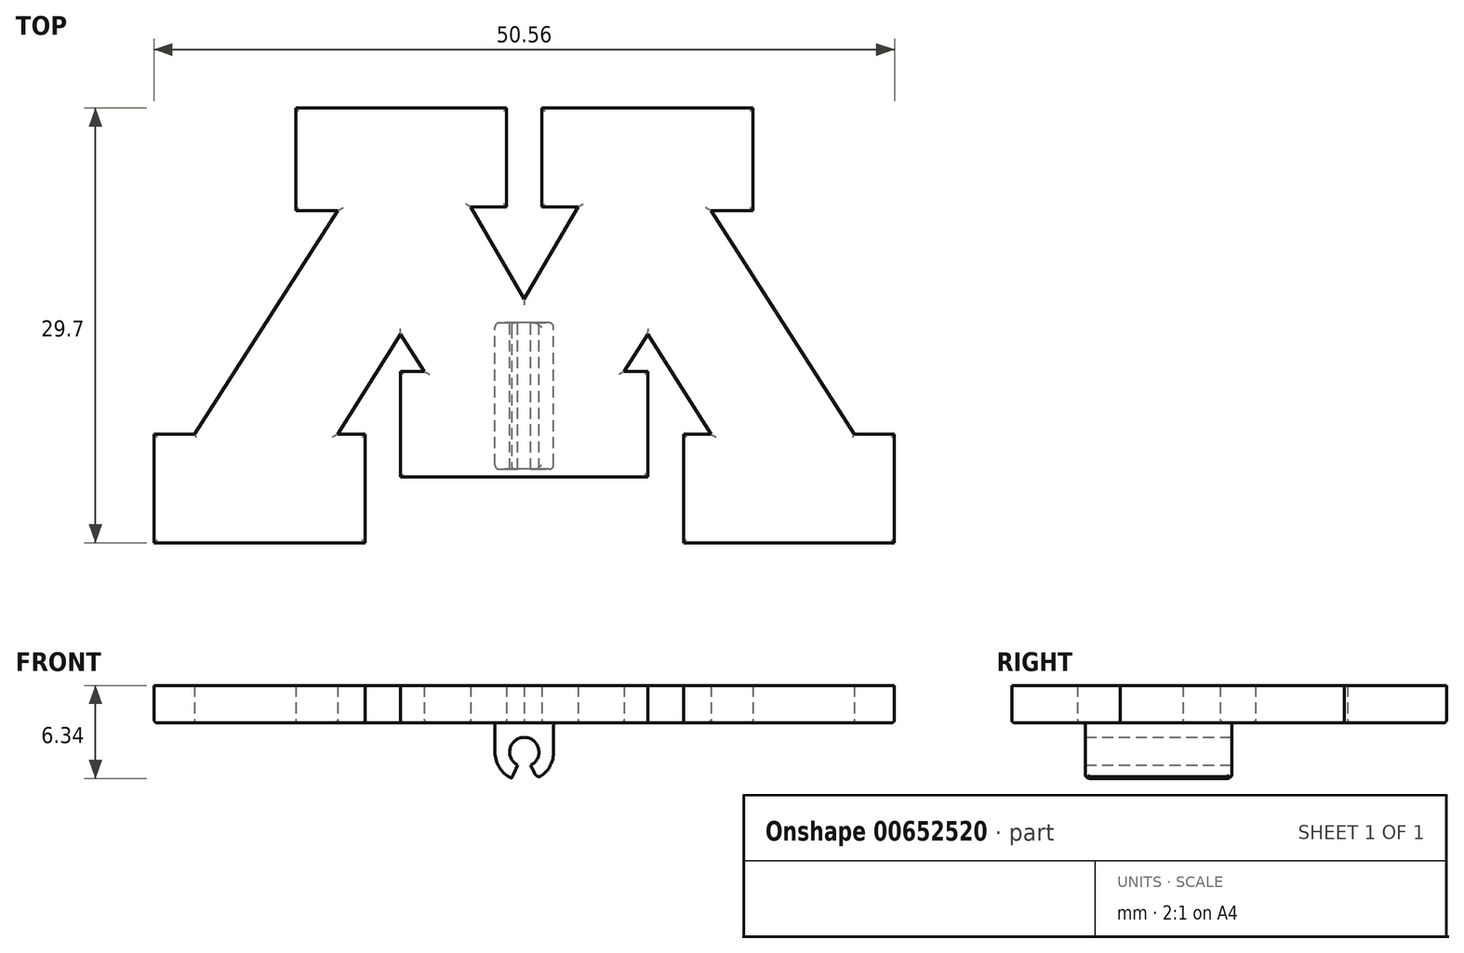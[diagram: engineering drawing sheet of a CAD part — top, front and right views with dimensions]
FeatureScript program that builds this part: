
annotation { "Feature Type Name" : "Feature", "Feature Type Description" : "" }
export const myFeature = defineFeature(function(context is Context, id is Id, definition is map)
    precondition{}
    {
        {
            var Q0;
            Q0=qCreatedBy(makeId("Front.planeOp"),FACE);
            var sketch = newSketch(context, id + "F0", { "sketchPlane" : qUnion([Q0])});
            skCircle(sketch, "E0", {"center": v(0, 0) * mm, "radius": 1 * mm});
            skArc(sketch, "E1", {"start": v(-2, 0) * mm, "mid": v(0, -2) * mm, "end": v(2, 0) * mm});
            skLineSegment(sketch, "E2", {"start": v(-2, 0) * mm, "end": v(-2, 2) * mm});
            skLineSegment(sketch, "E3", {"start": v(-2, 2) * mm, "end": v(0, 2) * mm});
            skLineSegment(sketch, "E4.MirrorCS", {"start": v(2, 2) * mm, "end": v(0, 2) * mm});
            skLineSegment(sketch, "E5.MirrorCS", {"start": v(2, 0) * mm, "end": v(2, 2) * mm});
            skSolve(sketch);
        }
        {
            var Q0;
            Q0=makeQuery(id+"F0.imprint","IMPRINT",FACE,{"disambiguationData":[TD([[makeQuery(id+"F0.imprint","IMPRINT",EDGE,{"derivedFrom":sQuery(id+"F0.wireOp",EDGE,"E0")}),-1.0]])]});
            extrude(context, id + "F1", {"entities" : qUnion([Q0]), "endBound" : BoundingType.SYMMETRIC, "depth" : 10 * mm, "offsetDistance" : 25.4 * mm});
        }
        {
            var Q0;
            Q0=makeQuery(id+"F1.opExtrude","CAP_FACE",FACE,{"disambiguationData":[OSD([sQuery(id+"F0.wireOp",EDGE,"E0"),sQuery(id+"F0.wireOp",EDGE,"E1")])],"isStart":false});
            var sketch = newSketch(context, id + "F2", { "sketchPlane" : qUnion([Q0])});
            skLineSegment(sketch, "E6", {"start": v(0, 0) * mm, "end": v(-0.87, -1.8) * mm});
            skLineSegment(sketch, "E7.MirrorCS", {"start": v(0, 0) * mm, "end": v(0.87, -1.8) * mm});
            skArc(sketch, "E8", {"start": v(-0.87, -1.8) * mm, "mid": v(0, -2) * mm, "end": v(0.87, -1.8) * mm});
            skSolve(sketch);
        }
        {
            var Q0;
            Q0=qSketchRegion(id+"F2",true);
            extrude(context, id + "F3", {"entities" : qUnion([Q0]), "operationType" : NewBodyOperationType.REMOVE, "endBound" : BoundingType.THROUGH_ALL, "oppositeDirection" : true, "depth" : 25 * mm, "offsetDistance" : 25 * mm});
        }
        {
            var Q0;
            Q0=makeQuery(id+"F3.boolean.opBoolean","COPY",EDGE,{"derivedFrom":makeQuery(id+"F3.opExtrude","SWEPT_EDGE",EDGE,{"disambiguationData":[OSD([sQuery(id+"F0.wireOp",EDGE,"E1"),sQuery(id+"F2.wireOp",EDGE,"E6"),sQuery(id+"F2.wireOp",EDGE,"E8")])]})});
            var Q1;
            Q1=makeQuery(id+"F3.boolean.opBoolean","COPY",EDGE,{"derivedFrom":makeQuery(id+"F3.opExtrude","SWEPT_EDGE",EDGE,{"disambiguationData":[OSD([sQuery(id+"F0.wireOp",EDGE,"E1"),sQuery(id+"F2.wireOp",EDGE,"E7.MirrorCS"),sQuery(id+"F2.wireOp",EDGE,"E8")])]})});
            var Q2;
            {var subQ0=sQuery(id+"F0.wireOp",EDGE,"E2");var subQ1=sQuery(id+"F0.wireOp",EDGE,"E1");Q2=makeQuery(id+"F3.boolean.opBoolean","SPLIT",EDGE,{"disambiguationData":[TD([makeQuery(id+"F1.opExtrude","SWEPT_FACE",FACE,{"disambiguationData":[OSD([subQ0])]})])],"derivedFrom":makeQuery(id+"F1.opExtrude","CAP_EDGE",EDGE,{"disambiguationData":[OSD([subQ1])],"isStart":false})});}
            var Q3;
            Q3=makeQuery(id+"F1.opExtrude","CAP_EDGE",EDGE,{"disambiguationData":[OSD([sQuery(id+"F0.wireOp",EDGE,"E2")])],"isStart":false});
            var Q4;
            {var subQ0=sQuery(id+"F0.wireOp",EDGE,"E5.MirrorCS");var subQ1=sQuery(id+"F0.wireOp",EDGE,"E1");Q4=makeQuery(id+"F3.boolean.opBoolean","SPLIT",EDGE,{"disambiguationData":[TD([makeQuery(id+"F1.opExtrude","SWEPT_FACE",FACE,{"disambiguationData":[OSD([subQ0])]})])],"derivedFrom":makeQuery(id+"F1.opExtrude","CAP_EDGE",EDGE,{"disambiguationData":[OSD([subQ1])],"isStart":false})});}
            var Q5;
            {var subQ0=sQuery(id+"F0.wireOp",EDGE,"E5.MirrorCS");var subQ1=sQuery(id+"F0.wireOp",EDGE,"E1");Q5=makeQuery(id+"F3.boolean.opBoolean","SPLIT",EDGE,{"disambiguationData":[TD([makeQuery(id+"F1.opExtrude","SWEPT_FACE",FACE,{"disambiguationData":[OSD([subQ0])]})])],"derivedFrom":makeQuery(id+"F1.opExtrude","CAP_EDGE",EDGE,{"disambiguationData":[OSD([subQ1])],"isStart":true})});}
            var Q6;
            Q6=makeQuery(id+"F1.opExtrude","CAP_EDGE",EDGE,{"disambiguationData":[OSD([sQuery(id+"F0.wireOp",EDGE,"E5.MirrorCS")])],"isStart":true});
            var Q7;
            {var subQ0=sQuery(id+"F0.wireOp",EDGE,"E2");var subQ1=sQuery(id+"F0.wireOp",EDGE,"E1");Q7=makeQuery(id+"F3.boolean.opBoolean","SPLIT",EDGE,{"disambiguationData":[TD([makeQuery(id+"F1.opExtrude","SWEPT_FACE",FACE,{"disambiguationData":[OSD([subQ0])]})])],"derivedFrom":makeQuery(id+"F1.opExtrude","CAP_EDGE",EDGE,{"disambiguationData":[OSD([subQ1])],"isStart":true})});}
            var Q8;
            Q8=makeQuery(id+"F1.opExtrude","CAP_EDGE",EDGE,{"disambiguationData":[OSD([sQuery(id+"F0.wireOp",EDGE,"E2")])],"isStart":true});
            fillet(context, id + "F4", {"entities" : qUnion([Q0, Q1, Q2, Q3, Q4, Q5, Q6, Q7, Q8]), "radius" : .3 * mm, "tangentPropagation" : true, "allowEdgeOverflow" : false});
        }
        {
            var Q0;
            Q0=makeQuery(id+"F1.opExtrude","SWEPT_FACE",FACE,{"disambiguationData":[OSD([sQuery(id+"F0.wireOp",EDGE,"E3"),sQuery(id+"F0.wireOp",EDGE,"E4.MirrorCS")])]});
            var sketch = newSketch(context, id + "F5", { "sketchPlane" : qUnion([Q0])});
            skLineSegment(sketch, "E9", {"start": v(-15.61, 19.67) * mm, "end": v(-1.2, 19.67) * mm});
            skLineSegment(sketch, "E10", {"start": v(-1.2, 19.67) * mm, "end": v(-1.2, 12.92) * mm});
            skLineSegment(sketch, "E11", {"start": v(-1.2, 12.92) * mm, "end": v(-3.66, 12.92) * mm});
            skLineSegment(sketch, "E12", {"start": v(-3.66, 12.92) * mm, "end": v(0, 6.63) * mm});
            skLineSegment(sketch, "E13", {"start": v(-15.61, 19.67) * mm, "end": v(-15.61, 12.67) * mm});
            skLineSegment(sketch, "E14", {"start": v(-15.61, 12.67) * mm, "end": v(-12.74, 12.67) * mm});
            skLineSegment(sketch, "E15", {"start": v(-12.74, 12.67) * mm, "end": v(-22.53, -2.61) * mm});
            skLineSegment(sketch, "E16", {"start": v(-22.53, -2.61) * mm, "end": v(-25.28, -2.61) * mm});
            skLineSegment(sketch, "E17", {"start": v(-25.28, -2.61) * mm, "end": v(-25.28, -10.03) * mm});
            skLineSegment(sketch, "E18", {"start": v(-25.28, -10.03) * mm, "end": v(-10.87, -10.03) * mm});
            skLineSegment(sketch, "E19", {"start": v(-10.87, -10.03) * mm, "end": v(-10.87, -2.61) * mm});
            skLineSegment(sketch, "E20", {"start": v(-10.87, -2.61) * mm, "end": v(-12.74, -2.61) * mm});
            skLineSegment(sketch, "E21", {"start": v(-12.74, -2.61) * mm, "end": v(-8.45, 4.22) * mm});
            skLineSegment(sketch, "E22", {"start": v(-8.45, 4.22) * mm, "end": v(-6.83, 1.68) * mm});
            skLineSegment(sketch, "E23", {"start": v(-6.83, 1.68) * mm, "end": v(-8.45, 1.68) * mm});
            skLineSegment(sketch, "E24", {"start": v(-8.45, 1.68) * mm, "end": v(-8.45, -5.53) * mm});
            skLineSegment(sketch, "E25", {"start": v(-8.45, -5.53) * mm, "end": v(0, -5.53) * mm});
            skLineSegment(sketch, "E26.MirrorCS", {"start": v(10.87, -10.03) * mm, "end": v(10.87, -2.61) * mm});
            skLineSegment(sketch, "E27.MirrorCS", {"start": v(22.53, -2.61) * mm, "end": v(25.28, -2.61) * mm});
            skLineSegment(sketch, "E28.MirrorCS", {"start": v(12.74, 12.67) * mm, "end": v(22.53, -2.61) * mm});
            skLineSegment(sketch, "E29.MirrorCS", {"start": v(3.66, 12.92) * mm, "end": v(0, 6.63) * mm});
            skLineSegment(sketch, "E30.MirrorCS", {"start": v(1.2, 19.67) * mm, "end": v(1.2, 12.92) * mm});
            skLineSegment(sketch, "E31.MirrorCS", {"start": v(25.28, -10.03) * mm, "end": v(10.87, -10.03) * mm});
            skLineSegment(sketch, "E32.MirrorCS", {"start": v(8.45, -5.53) * mm, "end": v(0, -5.53) * mm});
            skLineSegment(sketch, "E33.MirrorCS", {"start": v(1.2, 12.92) * mm, "end": v(3.66, 12.92) * mm});
            skLineSegment(sketch, "E34.MirrorCS", {"start": v(8.45, 1.68) * mm, "end": v(8.45, -5.53) * mm});
            skLineSegment(sketch, "E35.MirrorCS", {"start": v(25.28, -2.61) * mm, "end": v(25.28, -10.03) * mm});
            skLineSegment(sketch, "E36.MirrorCS", {"start": v(15.61, 19.67) * mm, "end": v(1.2, 19.67) * mm});
            skLineSegment(sketch, "E37.MirrorCS", {"start": v(12.74, -2.61) * mm, "end": v(8.45, 4.22) * mm});
            skLineSegment(sketch, "E38.MirrorCS", {"start": v(10.87, -2.61) * mm, "end": v(12.74, -2.61) * mm});
            skLineSegment(sketch, "E39.MirrorCS", {"start": v(15.61, 12.67) * mm, "end": v(12.74, 12.67) * mm});
            skLineSegment(sketch, "E40.MirrorCS", {"start": v(15.61, 19.67) * mm, "end": v(15.61, 12.67) * mm});
            skLineSegment(sketch, "E41.MirrorCS", {"start": v(6.83, 1.68) * mm, "end": v(8.45, 1.68) * mm});
            skLineSegment(sketch, "E42.MirrorCS", {"start": v(8.45, 4.22) * mm, "end": v(6.83, 1.68) * mm});
            skSolve(sketch);
        }
        {
            var Q0;
            Q0=makeQuery(id+"F5.imprint","IMPRINT",FACE,{"disambiguationData":[TD([[makeQuery(id+"F5.imprint","IMPRINT",EDGE,{"derivedFrom":sQuery(id+"F5.wireOp",EDGE,"E9")}),-1.0]])]});
            var Q1;
            {var subQ1=sQuery(id+"F0.wireOp",EDGE,"E3");var subQ3=sQuery(id+"F0.wireOp",EDGE,"E2");Q1=makeQuery(id+"F5.imprint","IMPRINT",FACE,{"disambiguationData":[TD([[makeQuery(id+"F5.imprint","IMPRINT",EDGE,{"derivedFrom":makeQuery(id+"F1.opExtrude","SWEPT_EDGE",EDGE,{"disambiguationData":[OSD([subQ3,subQ1])]})}),-1.0]])]});}
            extrude(context, id + "F6", {"entities" : qUnion([Q0, Q1]), "operationType" : NewBodyOperationType.ADD, "depth" : 2.54 * mm, "offsetDistance" : 25 * mm});
        }
        {
            var Q0;
            Q0=makeQuery(id+"F6.opExtrude","CAP_FACE",FACE,{"disambiguationData":[OSD([sQuery(id+"F5.wireOp",EDGE,"E9"),sQuery(id+"F5.wireOp",EDGE,"E10"),sQuery(id+"F5.wireOp",EDGE,"E11"),sQuery(id+"F5.wireOp",EDGE,"E12"),sQuery(id+"F5.wireOp",EDGE,"E13"),sQuery(id+"F5.wireOp",EDGE,"E14"),sQuery(id+"F5.wireOp",EDGE,"E15"),sQuery(id+"F5.wireOp",EDGE,"E16"),sQuery(id+"F5.wireOp",EDGE,"E17"),sQuery(id+"F5.wireOp",EDGE,"E18"),sQuery(id+"F5.wireOp",EDGE,"E19"),sQuery(id+"F5.wireOp",EDGE,"E20"),sQuery(id+"F5.wireOp",EDGE,"E21"),sQuery(id+"F5.wireOp",EDGE,"E22"),sQuery(id+"F5.wireOp",EDGE,"E23"),sQuery(id+"F5.wireOp",EDGE,"E24"),sQuery(id+"F5.wireOp",EDGE,"E25"),sQuery(id+"F5.wireOp",EDGE,"E26.MirrorCS"),sQuery(id+"F5.wireOp",EDGE,"E27.MirrorCS"),sQuery(id+"F5.wireOp",EDGE,"E28.MirrorCS"),sQuery(id+"F5.wireOp",EDGE,"E29.MirrorCS"),sQuery(id+"F5.wireOp",EDGE,"E30.MirrorCS"),sQuery(id+"F5.wireOp",EDGE,"E31.MirrorCS"),sQuery(id+"F5.wireOp",EDGE,"E32.MirrorCS"),sQuery(id+"F5.wireOp",EDGE,"E33.MirrorCS"),sQuery(id+"F5.wireOp",EDGE,"E34.MirrorCS"),sQuery(id+"F5.wireOp",EDGE,"E35.MirrorCS"),sQuery(id+"F5.wireOp",EDGE,"E36.MirrorCS"),sQuery(id+"F5.wireOp",EDGE,"E37.MirrorCS"),sQuery(id+"F5.wireOp",EDGE,"E38.MirrorCS"),sQuery(id+"F5.wireOp",EDGE,"E39.MirrorCS"),sQuery(id+"F5.wireOp",EDGE,"E40.MirrorCS"),sQuery(id+"F5.wireOp",EDGE,"E41.MirrorCS"),sQuery(id+"F5.wireOp",EDGE,"E42.MirrorCS")])],"isStart":true});
            fillet(context, id + "F7", {"entities" : qUnion([Q0]), "radius" : 0.2 * mm, "tangentPropagation" : true, "allowEdgeOverflow" : false});
        }
    });
